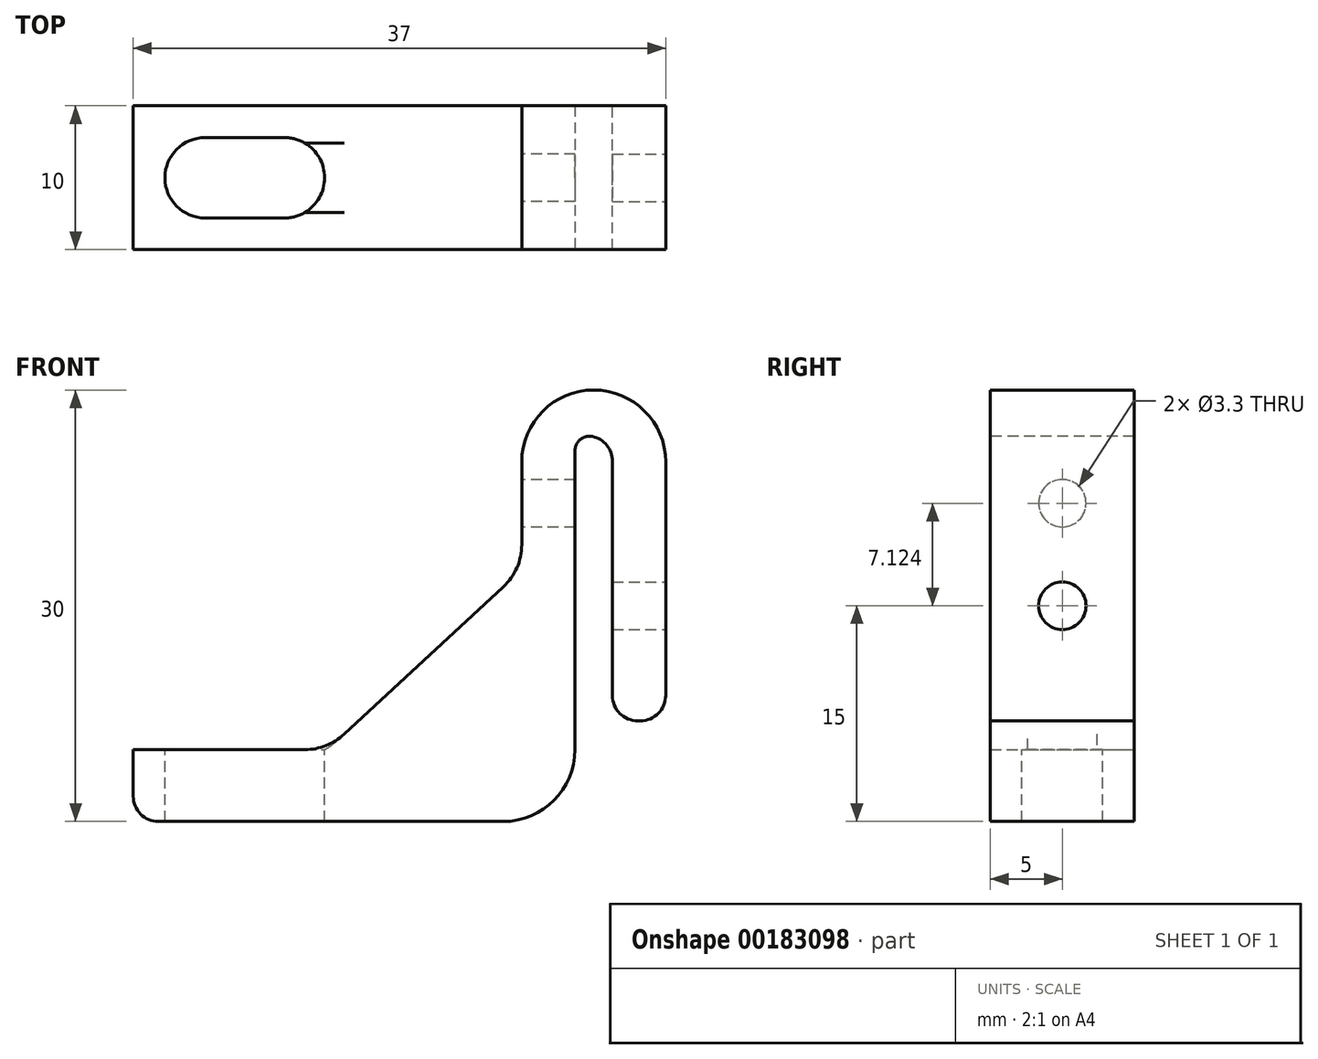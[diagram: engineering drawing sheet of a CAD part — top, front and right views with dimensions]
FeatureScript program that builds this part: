
annotation { "Feature Type Name" : "Feature", "Feature Type Description" : "" }
export const myFeature = defineFeature(function(context is Context, id is Id, definition is map)
    precondition{}
    {
        {
            var Q0;
            Q0=qCreatedBy(makeId("Front.planeOp"),FACE);
            var sketch = newSketch(context, id + "F0", { "sketchPlane" : qUnion([Q0])});
            skLineSegment(sketch, "E0", {"start": v(0, 0) * mm, "end": v(0, 15) * mm});
            skLineSegment(sketch, "E1", {"start": v(0, 15) * mm, "end": v(-10, 15) * mm});
            skLineSegment(sketch, "E2", {"start": v(-10, 15) * mm, "end": v(-10, -10) * mm});
            skLineSegment(sketch, "E3", {"start": v(-10, -10) * mm, "end": v(-37, -10) * mm});
            skLineSegment(sketch, "E4", {"start": v(-37, -10) * mm, "end": v(-37, -15) * mm});
            skLineSegment(sketch, "E5", {"start": v(-37, -15) * mm, "end": v(0, -15) * mm});
            skLineSegment(sketch, "E6", {"start": v(0, -15) * mm, "end": v(0, 0) * mm});
            skLineSegment(sketch, "E7", {"start": v(-5, 15) * mm, "end": v(-5, -15) * mm});
            skLineSegment(sketch, "E8", {"start": v(-5, 15) * mm, "end": v(-5, 11.8) * mm});
            skLineSegment(sketch, "E9", {"start": v(-5, 11.8) * mm, "end": v(-6.3, 11.8) * mm});
            skLineSegment(sketch, "E10", {"start": v(-6.3, 11.8) * mm, "end": v(-6.3, -15) * mm});
            skLineSegment(sketch, "E11.MirrorCS", {"start": v(-5, 11.8) * mm, "end": v(-3.7, 11.8) * mm});
            skLineSegment(sketch, "E12.MirrorCS", {"start": v(-3.7, 11.8) * mm, "end": v(-3.7, -15) * mm});
            skLineSegment(sketch, "E13", {"start": v(-23.5, -10) * mm, "end": v(-10, 2.5) * mm});
            skLineSegment(sketch, "E14", {"start": v(-3.7, -15) * mm, "end": v(-3.7, -8) * mm});
            skLineSegment(sketch, "E15", {"start": v(-3.7, -8) * mm, "end": v(0, -8) * mm});
            skSolve(sketch);
        }
        {
            var Q0;
            {var subQ4=sQuery(id+"F0.wireOp",EDGE,"E0");Q0=makeQuery(id+"F0.imprint","IMPRINT",FACE,{"disambiguationData":[TD([[makeQuery(id+"F0.imprint","IMPRINT",EDGE,{"derivedFrom":subQ4}),1.0]])]});}
            var Q1;
            {var subQ2=sQuery(id+"F0.wireOp",EDGE,"E2");Q1=makeQuery(id+"F0.imprint","IMPRINT",FACE,{"disambiguationData":[TD([[makeQuery(id+"F0.imprint","IMPRINT",EDGE,{"derivedFrom":subQ2}),1.0]])]});}
            var Q2;
            {var subQ3=sQuery(id+"F0.wireOp",EDGE,"E13");Q2=makeQuery(id+"F0.imprint","IMPRINT",FACE,{"disambiguationData":[TD([[makeQuery(id+"F0.imprint","IMPRINT",EDGE,{"derivedFrom":subQ3}),-1.0]])]});}
            extrude(context, id + "F1", {"entities" : qUnion([Q0, Q1, Q2]), "depth" : 10 * mm});
        }
        {
            var Q0;
            Q0=makeQuery(id+"F1.opExtrude","SWEPT_FACE",FACE,{"disambiguationData":[OSD([sQuery(id+"F0.wireOp",EDGE,"E3")])]});
            var sketch = newSketch(context, id + "F2", { "sketchPlane" : qUnion([Q0])});
            skLineSegment(sketch, "E16", {"start": v(-37, -5) * mm, "end": v(-32, -5) * mm});
            skCircle(sketch, "E17", {"center": v(-32, -5) * mm, "radius": 2.8 * mm});
            skLineSegment(sketch, "E18", {"start": v(-32, -5) * mm, "end": v(-26.5, -5) * mm});
            skCircle(sketch, "E19", {"center": v(-26.5, -5) * mm, "radius": 2.8 * mm});
            skLineSegment(sketch, "E20", {"start": v(-32, -2.2) * mm, "end": v(-26.5, -2.2) * mm});
            skLineSegment(sketch, "E21", {"start": v(-32, -7.8) * mm, "end": v(-26.5, -7.8) * mm});
            skSolve(sketch);
        }
        {
            var Q0;
            Q0=makeQuery(id+"F1.opExtrude","SWEPT_EDGE",EDGE,{"disambiguationData":[OSD([sQuery(id+"F0.wireOp",EDGE,"E1"),sQuery(id+"F0.wireOp",EDGE,"E2")])]});
            var Q1;
            Q1=makeQuery(id+"F1.opExtrude","SWEPT_EDGE",EDGE,{"disambiguationData":[OSD([sQuery(id+"F0.wireOp",EDGE,"E0"),sQuery(id+"F0.wireOp",EDGE,"E1")])]});
            var Q2;
            Q2=makeQuery(id+"F1.opExtrude","SWEPT_EDGE",EDGE,{"disambiguationData":[OSD([sQuery(id+"F0.wireOp",EDGE,"E5"),sQuery(id+"F0.wireOp",EDGE,"E10")])]});
            fillet(context, id + "F3", {"entities" : qUnion([Q0, Q1, Q2]), "radius" : 5 * mm, "tangentPropagation" : true, "allowEdgeOverflow" : false});
        }
        {
            var Q0;
            Q0=makeQuery(id+"F2.imprint","IMPRINT",FACE,{"disambiguationData":[TD([[makeQuery(id+"F2.imprint","IMPRINT",EDGE,{"derivedFrom":sQuery(id+"F2.wireOp",EDGE,"E17")}),1.0]])]});
            var Q1;
            {var subQ0=sQuery(id+"F2.wireOp",EDGE,"E19");var subQ1=makeQuery(id+"F2.imprint","INTERSECT",VERTEX,{"derivedFrom":[subQ0,sQuery(id+"F2.wireOp",EDGE,"E20")]});Q1=makeQuery(id+"F2.imprint","IMPRINT",FACE,{"disambiguationData":[TD([[makeQuery(id+"F2.imprint","IMPRINT",EDGE,{"disambiguationData":[TD([[subQ1,-1.0]])],"derivedFrom":subQ0}),1.0]])]});}
            var Q2;
            {var subQ0=sQuery(id+"F2.wireOp",EDGE,"E20");Q2=makeQuery(id+"F2.imprint","IMPRINT",FACE,{"disambiguationData":[TD([[makeQuery(id+"F2.imprint","IMPRINT",EDGE,{"derivedFrom":subQ0}),-1.0]])]});}
            var Q3;
            {var subQ0=sQuery(id+"F2.wireOp",EDGE,"E21");Q3=makeQuery(id+"F2.imprint","IMPRINT",FACE,{"disambiguationData":[TD([[makeQuery(id+"F2.imprint","IMPRINT",EDGE,{"derivedFrom":subQ0}),1.0]])]});}
            var Q4;
            {var subQ0=sQuery(id+"F2.wireOp",EDGE,"E18");var subQ1=sQuery(id+"F2.wireOp",EDGE,"E17");var subQ2=makeQuery(id+"F2.imprint","INTERSECT",VERTEX,{"derivedFrom":[subQ1,subQ0]});Q4=makeQuery(id+"F2.imprint","IMPRINT",FACE,{"disambiguationData":[TD([[makeQuery(id+"F2.imprint","IMPRINT",EDGE,{"disambiguationData":[TD([[subQ2,-1.0]])],"derivedFrom":subQ1}),1.0]])]});}
            var Q5;
            {var subQ0=sQuery(id+"F2.wireOp",EDGE,"E18");var subQ1=sQuery(id+"F2.wireOp",EDGE,"E17");var subQ2=makeQuery(id+"F2.imprint","INTERSECT",VERTEX,{"derivedFrom":[subQ1,subQ0]});Q5=makeQuery(id+"F2.imprint","IMPRINT",FACE,{"disambiguationData":[TD([[makeQuery(id+"F2.imprint","IMPRINT",EDGE,{"disambiguationData":[TD([[subQ2,1.0]])],"derivedFrom":subQ1}),1.0]])]});}
            extrude(context, id + "F4", {"entities" : qUnion([Q0, Q1, Q2, Q3, Q4, Q5]), "operationType" : NewBodyOperationType.REMOVE, "oppositeDirection" : true, "depth" : 25 * mm});
        }
        {
            var Q0;
            Q0=makeQuery(id+"F1.opExtrude","SWEPT_EDGE",EDGE,{"disambiguationData":[OSD([sQuery(id+"F0.wireOp",EDGE,"E4"),sQuery(id+"F0.wireOp",EDGE,"E5")])]});
            var Q1;
            Q1=makeQuery(id+"F1.opExtrude","SWEPT_EDGE",EDGE,{"disambiguationData":[OSD([sQuery(id+"F0.wireOp",EDGE,"E5"),sQuery(id+"F0.wireOp",EDGE,"E12.MirrorCS")])]});
            var Q2;
            Q2=makeQuery(id+"F1.opExtrude","SWEPT_EDGE",EDGE,{"disambiguationData":[OSD([sQuery(id+"F0.wireOp",EDGE,"E5"),sQuery(id+"F0.wireOp",EDGE,"E6")])]});
            var Q3;
            Q3=makeQuery(id+"F1.opExtrude","SWEPT_EDGE",EDGE,{"disambiguationData":[OSD([sQuery(id+"F0.wireOp",EDGE,"E12.MirrorCS"),sQuery(id+"F0.wireOp",EDGE,"E14"),sQuery(id+"F0.wireOp",EDGE,"E15")])]});
            fillet(context, id + "F5", {"entities" : qUnion([Q0, Q1, Q2, Q3]), "radius" : 1.75 * mm, "tangentPropagation" : true, "allowEdgeOverflow" : false});
        }
        {
            var Q0;
            Q0=makeQuery(id+"F1.opExtrude","SWEPT_EDGE",EDGE,{"disambiguationData":[OSD([sQuery(id+"F0.wireOp",EDGE,"E2"),sQuery(id+"F0.wireOp",EDGE,"E13")])]});
            var Q1;
            Q1=makeQuery(id+"F1.opExtrude","SWEPT_EDGE",EDGE,{"disambiguationData":[OSD([sQuery(id+"F0.wireOp",EDGE,"E3"),sQuery(id+"F0.wireOp",EDGE,"E13")])]});
            fillet(context, id + "F6", {"entities" : qUnion([Q0, Q1]), "radius" : 4 * mm, "tangentPropagation" : true, "allowEdgeOverflow" : false});
        }
        {
            var Q0;
            Q0=makeQuery(id+"F1.opExtrude","SWEPT_EDGE",EDGE,{"disambiguationData":[OSD([sQuery(id+"F0.wireOp",EDGE,"E11.MirrorCS"),sQuery(id+"F0.wireOp",EDGE,"E12.MirrorCS")])]});
            var Q1;
            Q1=makeQuery(id+"F1.opExtrude","SWEPT_EDGE",EDGE,{"disambiguationData":[OSD([sQuery(id+"F0.wireOp",EDGE,"E9"),sQuery(id+"F0.wireOp",EDGE,"E10")])]});
            fillet(context, id + "F7", {"entities" : qUnion([Q0, Q1]), "radius" : 1 * mm, "tangentPropagation" : true, "allowEdgeOverflow" : false});
        }
        {
            var Q0;
            Q0=makeQuery(id+"F1.opExtrude","SWEPT_FACE",FACE,{"disambiguationData":[OSD([sQuery(id+"F0.wireOp",EDGE,"E2")])]});
            var sketch = newSketch(context, id + "F8", { "sketchPlane" : qUnion([Q0])});
            skLineSegment(sketch, "E22", {"start": v(5, 10) * mm, "end": v(5, 4.25) * mm});
            skLineSegment(sketch, "E23", {"start": v(5, 4.25) * mm, "end": v(5, 7.12) * mm});
            skCircle(sketch, "E24", {"center": v(5, 7.12) * mm, "radius": 1.65 * mm});
            skSolve(sketch);
        }
        {
            var Q0;
            Q0 = qSketchRegion(id + "F8", true);
            extrude(context, id + "F9", {"entities" : qUnion([Q0]), "operationType" : NewBodyOperationType.REMOVE, "oppositeDirection" : true, "depth" : 5 * mm});
        }
        {
            var Q0;
            Q0=makeQuery(id+"F1.opExtrude","SWEPT_FACE",FACE,{"disambiguationData":[OSD([sQuery(id+"F0.wireOp",EDGE,"E0"),sQuery(id+"F0.wireOp",EDGE,"E6")])]});
            var sketch = newSketch(context, id + "F10", { "sketchPlane" : qUnion([Q0])});
            skLineSegment(sketch, "E25", {"start": v(-5, -6.25) * mm, "end": v(-5, 0) * mm});
            skCircle(sketch, "E26", {"center": v(-5, 0) * mm, "radius": 1.65 * mm});
            skSolve(sketch);
        }
        {
            var Q0;
            Q0=makeQuery(id+"F10.imprint","IMPRINT",FACE,{"disambiguationData":[TD([[makeQuery(id+"F10.imprint","IMPRINT",EDGE,{"derivedFrom":sQuery(id+"F10.wireOp",EDGE,"E26")}),1.0]])]});
            extrude(context, id + "F11", {"entities" : qUnion([Q0]), "operationType" : NewBodyOperationType.REMOVE, "oppositeDirection" : true, "depth" : 5 * mm});
        }
    });
